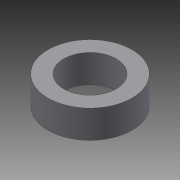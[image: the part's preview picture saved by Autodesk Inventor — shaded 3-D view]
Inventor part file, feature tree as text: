
AUTODESK INVENTOR PART (.ipt)
format: ipt  version: 2014 (Build 180170000, 170)  size: 74,752 bytes
history: native  units: mm
features: other x1, extrude x1, sketch x1
ambient origin geometry x8: Origin, YZ Plane, XZ Plane, XY Plane, X Axis, Y Axis, Z Axis, Center Point
bodies: Body1 (feature_tree)
feature tree (3):
  other  "Твердое тело1"
  extrude  "Выдавливание1"  Depth=7.5mm
  sketch  "Эскиз1"
